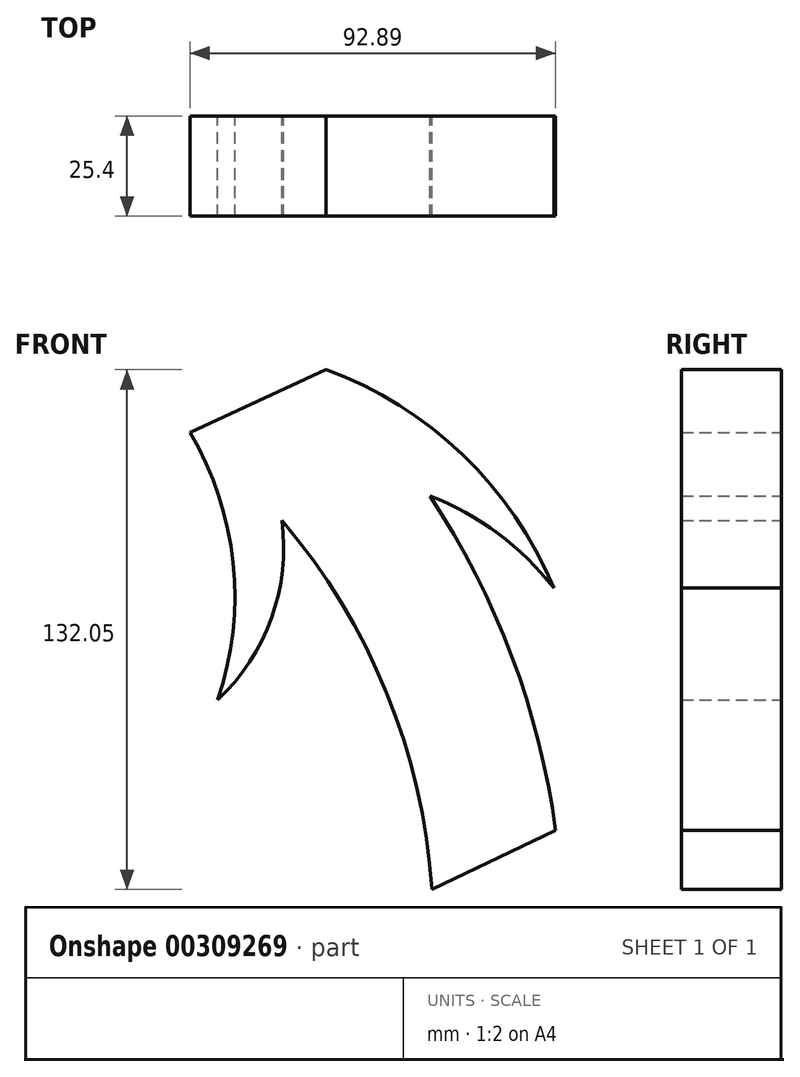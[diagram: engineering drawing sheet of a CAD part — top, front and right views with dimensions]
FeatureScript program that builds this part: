
annotation { "Feature Type Name" : "Feature", "Feature Type Description" : "" }
export const myFeature = defineFeature(function(context is Context, id is Id, definition is map)
    precondition{}
    {
        {
            var Q0;
            Q0=qCreatedBy(makeId("Front.planeOp"),FACE);
            var sketch = newSketch(context, id + "F0", { "sketchPlane" : qUnion([Q0])});
            skArc(sketch, "E0", {"start": v(9.84, -70.96) * mm, "mid": v(-8.5, -6.34) * mm, "end": v(-51.63, 45.15) * mm});
            skArc(sketch, "E1", {"start": v(41.26, -55.93) * mm, "mid": v(21.8, 7.4) * mm, "end": v(-17.02, 61.1) * mm});
            skLineSegment(sketch, "E2", {"start": v(41.26, -55.93) * mm, "end": v(9.84, -70.96) * mm});
            skLineSegment(sketch, "E3", {"start": v(-51.63, 45.15) * mm, "end": v(-17.02, 61.1) * mm});
            skArc(sketch, "E4", {"start": v(40.79, 5.56) * mm, "mid": v(17.73, 39.42) * mm, "end": v(-17.02, 61.1) * mm});
            skArc(sketch, "E5", {"start": v(40.79, 5.56) * mm, "mid": v(26.68, 19.43) * mm, "end": v(9.35, 28.97) * mm});
            skArc(sketch, "E6", {"start": v(-44.56, -22.82) * mm, "mid": v(-40.65, 11.94) * mm, "end": v(-51.63, 45.15) * mm});
            skArc(sketch, "E7", {"start": v(-44.56, -22.82) * mm, "mid": v(-30.91, -2) * mm, "end": v(-28.24, 22.75) * mm});
            skSolve(sketch);
        }
        {
            var Q0;
            Q0 = qSketchRegion(id + "F0", true);
            extrude(context, id + "F1", {"entities" : qUnion([Q0]), "depth" : 25.4 * mm});
        }
    });
